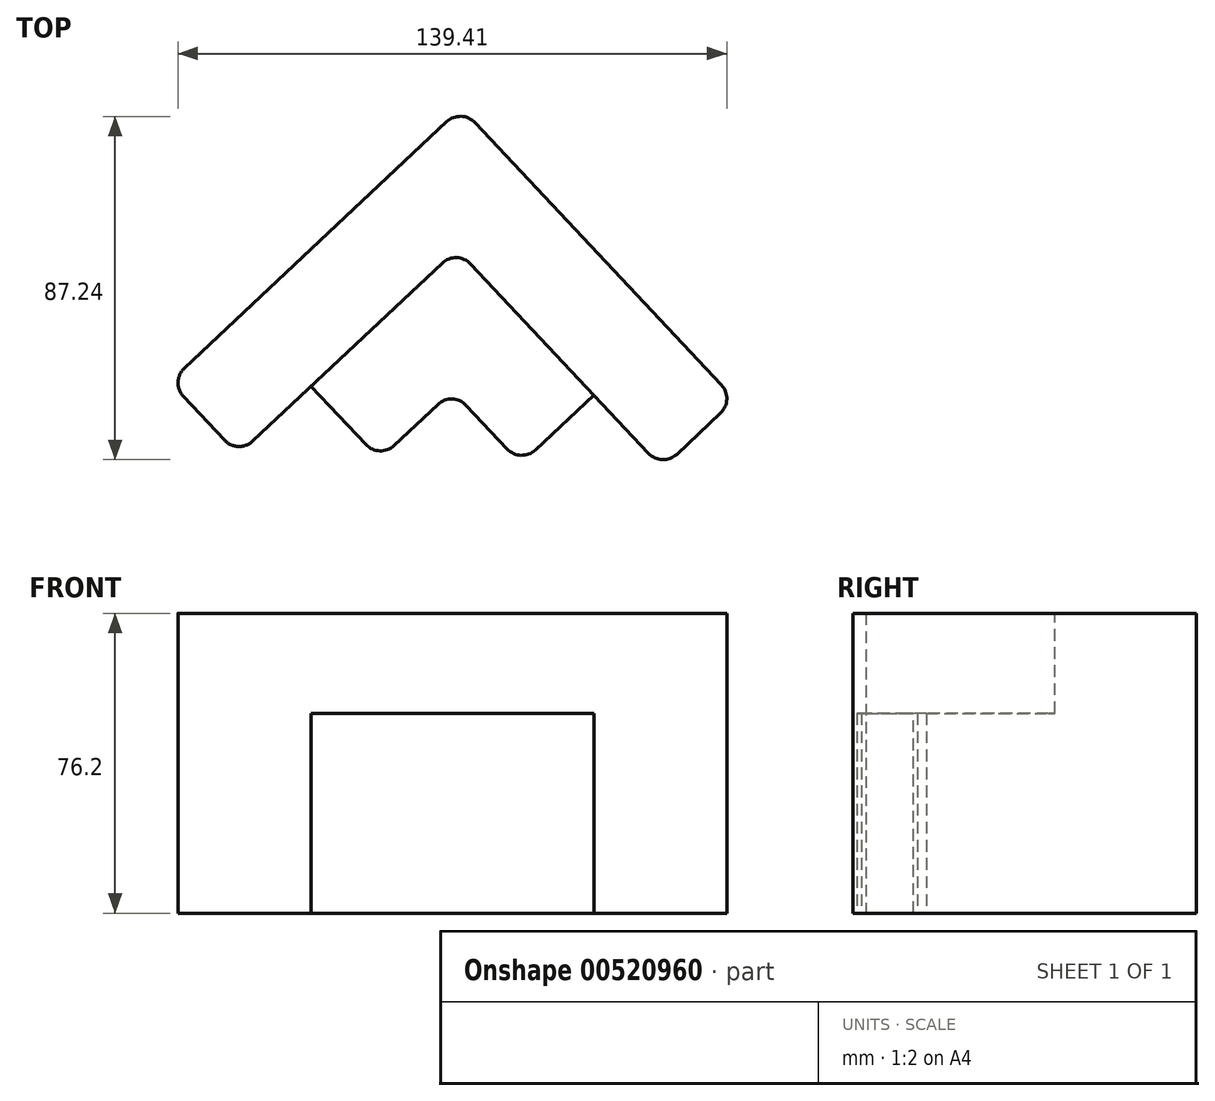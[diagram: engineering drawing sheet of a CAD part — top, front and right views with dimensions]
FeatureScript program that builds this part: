
annotation { "Feature Type Name" : "Feature", "Feature Type Description" : "" }
export const myFeature = defineFeature(function(context is Context, id is Id, definition is map)
    precondition{}
    {
        {
            var Q0;
            Q0=qCreatedBy(makeId("Top.planeOp"),FACE);
            var sketch = newSketch(context, id + "F0", { "sketchPlane" : qUnion([Q0])});
            skLineSegment(sketch, "E0", {"start": v(0, 53.43) * mm, "end": v(69.56, -20.62) * mm});
            skLineSegment(sketch, "E1", {"start": v(0, 53.43) * mm, "end": v(-74.05, -16.13) * mm});
            skLineSegment(sketch, "E2", {"start": v(169.5, -71.15) * mm, "end": v(169.5, -71.15) * mm});
            skLineSegment(sketch, "E3", {"start": v(-74.05, -16.13) * mm, "end": v(-56.66, -34.64) * mm});
            skLineSegment(sketch, "E4", {"start": v(-56.66, -34.64) * mm, "end": v(-38.15, -17.25) * mm});
            skLineSegment(sketch, "E5", {"start": v(-38.15, -17.25) * mm, "end": v(-20.76, -35.76) * mm});
            skLineSegment(sketch, "E6", {"start": v(-20.76, -35.76) * mm, "end": v(-2.24, -18.37) * mm});
            skLineSegment(sketch, "E7", {"start": v(-2.24, -18.37) * mm, "end": v(15.15, -36.89) * mm});
            skLineSegment(sketch, "E8", {"start": v(15.15, -36.89) * mm, "end": v(33.66, -19.5) * mm});
            skLineSegment(sketch, "E9", {"start": v(33.66, -19.5) * mm, "end": v(51.05, -38) * mm});
            skLineSegment(sketch, "E10", {"start": v(69.56, -20.62) * mm, "end": v(51.05, -38) * mm});
            skSolve(sketch);
        }
        {
            var Q0;
            Q0=makeQuery(id+"F0.imprint","IMPRINT",FACE,{"disambiguationData":[TD([[makeQuery(id+"F0.imprint","IMPRINT",EDGE,{"derivedFrom":sQuery(id+"F0.wireOp",EDGE,"E0")}),-1.0]])]});
            extrude(context, id + "F1", {"entities" : qUnion([Q0]), "depth" : 25.4 * mm, "offsetDistance" : 25.4 * mm});
        }
        {
            var Q0;
            Q0=makeQuery(id+"F1.opExtrude","CAP_FACE",FACE,{"disambiguationData":[OSD([sQuery(id+"F0.wireOp",EDGE,"E0"),sQuery(id+"F0.wireOp",EDGE,"E1"),sQuery(id+"F0.wireOp",EDGE,"E3"),sQuery(id+"F0.wireOp",EDGE,"E4"),sQuery(id+"F0.wireOp",EDGE,"E5"),sQuery(id+"F0.wireOp",EDGE,"E6"),sQuery(id+"F0.wireOp",EDGE,"E7"),sQuery(id+"F0.wireOp",EDGE,"E8"),sQuery(id+"F0.wireOp",EDGE,"E9"),sQuery(id+"F0.wireOp",EDGE,"E10")])],"isStart":false});
            var sketch = newSketch(context, id + "F2", { "sketchPlane" : qUnion([Q0])});
            skLineSegment(sketch, "E11", {"start": v(-38.15, -17.25) * mm, "end": v(-1.12, 17.53) * mm});
            skLineSegment(sketch, "E12", {"start": v(-1.12, 17.53) * mm, "end": v(33.66, -19.5) * mm});
            skSolve(sketch);
        }
        {
            var Q0;
            Q0=makeQuery(id+"F2.imprint","IMPRINT",FACE,{"disambiguationData":[TD([[makeQuery(id+"F2.imprint","IMPRINT",EDGE,{"derivedFrom":sQuery(id+"F2.wireOp",EDGE,"E11")}),-1.0]])]});
            extrude(context, id + "F3", {"entities" : qUnion([Q0]), "operationType" : NewBodyOperationType.ADD, "depth" : 25.4 * mm, "offsetDistance" : 25.4 * mm});
        }
        {
            var Q0;
            Q0=makeQuery(id+"F1.opExtrude","CAP_FACE",FACE,{"disambiguationData":[OSD([sQuery(id+"F0.wireOp",EDGE,"E0"),sQuery(id+"F0.wireOp",EDGE,"E1"),sQuery(id+"F0.wireOp",EDGE,"E3"),sQuery(id+"F0.wireOp",EDGE,"E4"),sQuery(id+"F0.wireOp",EDGE,"E5"),sQuery(id+"F0.wireOp",EDGE,"E6"),sQuery(id+"F0.wireOp",EDGE,"E7"),sQuery(id+"F0.wireOp",EDGE,"E8"),sQuery(id+"F0.wireOp",EDGE,"E9"),sQuery(id+"F0.wireOp",EDGE,"E10")])],"isStart":false});
            var sketch = newSketch(context, id + "F4", { "sketchPlane" : qUnion([Q0])});
            skSolve(sketch);
        }
        {
            var Q0;
            Q0=makeQuery(id+"F4.imprint","IMPRINT",FACE,{"disambiguationData":[TD([[makeQuery(id+"F4.imprint","IMPRINT",EDGE,{"derivedFrom":makeQuery(id+"F1.opExtrude","CAP_EDGE",EDGE,{"disambiguationData":[OSD([sQuery(id+"F0.wireOp",EDGE,"E0")])],"isStart":false})}),-1.0]])]});
            extrude(context, id + "F5", {"entities" : qUnion([Q0]), "operationType" : NewBodyOperationType.ADD, "depth" : 50.8 * mm, "offsetDistance" : 25.4 * mm});
        }
        {
            var Q0;
            Q0=makeQuery(id+"F5.opExtrude","SWEPT_EDGE",EDGE,{"disambiguationData":[OSD([sQuery(id+"F2.wireOp",EDGE,"E11"),sQuery(id+"F2.wireOp",EDGE,"E12")])]});
            fillet(context, id + "F6", {"entities" : qUnion([Q0]), "radius" : 5.08 * mm, "tangentPropagation" : true, "allowEdgeOverflow" : false});
        }
        {
            var Q0;
            {var subQ0=sQuery(id+"F0.wireOp",EDGE,"E7");var subQ1=sQuery(id+"F0.wireOp",EDGE,"E6");Q0=makeQuery(id+"F3.boolean.opBoolean","MERGE",EDGE,{"derivedFrom":[makeQuery(id+"F1.opExtrude","SWEPT_EDGE",EDGE,{"disambiguationData":[OSD([subQ1,subQ0])]}),makeQuery(id+"F3.opExtrude","SWEPT_EDGE",EDGE,{"disambiguationData":[OSD([subQ1,subQ0])]})]});}
            fillet(context, id + "F7", {"entities" : qUnion([Q0]), "radius" : 5.08 * mm, "tangentPropagation" : true, "allowEdgeOverflow" : false});
        }
        {
            var Q0;
            {var subQ0=sQuery(id+"F0.wireOp",EDGE,"E8");var subQ1=sQuery(id+"F0.wireOp",EDGE,"E7");Q0=makeQuery(id+"F3.boolean.opBoolean","MERGE",EDGE,{"derivedFrom":[makeQuery(id+"F1.opExtrude","SWEPT_EDGE",EDGE,{"disambiguationData":[OSD([subQ1,subQ0])]}),makeQuery(id+"F3.opExtrude","SWEPT_EDGE",EDGE,{"disambiguationData":[OSD([subQ1,subQ0])]})]});}
            fillet(context, id + "F8", {"entities" : qUnion([Q0]), "radius" : 5.08 * mm, "tangentPropagation" : true, "allowEdgeOverflow" : false});
        }
        {
            var Q0;
            {var subQ0=sQuery(id+"F0.wireOp",EDGE,"E6");var subQ1=sQuery(id+"F0.wireOp",EDGE,"E5");Q0=makeQuery(id+"F3.boolean.opBoolean","MERGE",EDGE,{"derivedFrom":[makeQuery(id+"F1.opExtrude","SWEPT_EDGE",EDGE,{"disambiguationData":[OSD([subQ1,subQ0])]}),makeQuery(id+"F3.opExtrude","SWEPT_EDGE",EDGE,{"disambiguationData":[OSD([subQ1,subQ0])]})]});}
            fillet(context, id + "F9", {"entities" : qUnion([Q0]), "radius" : 5.08 * mm, "tangentPropagation" : true, "allowEdgeOverflow" : false});
        }
        {
            var Q0;
            {var subQ0=sQuery(id+"F0.wireOp",EDGE,"E1");var subQ1=sQuery(id+"F0.wireOp",EDGE,"E0");Q0=makeQuery(id+"F5.boolean.opBoolean","MERGE",EDGE,{"derivedFrom":[makeQuery(id+"F1.opExtrude","SWEPT_EDGE",EDGE,{"disambiguationData":[OSD([subQ1,subQ0])]}),makeQuery(id+"F5.opExtrude","SWEPT_EDGE",EDGE,{"disambiguationData":[OSD([subQ1,subQ0])]})]});}
            fillet(context, id + "F10", {"entities" : qUnion([Q0]), "radius" : 5.08 * mm, "tangentPropagation" : true, "allowEdgeOverflow" : false});
        }
        {
            var Q0;
            {var subQ0=sQuery(id+"F0.wireOp",EDGE,"E3");var subQ1=sQuery(id+"F0.wireOp",EDGE,"E1");Q0=makeQuery(id+"F5.boolean.opBoolean","MERGE",EDGE,{"derivedFrom":[makeQuery(id+"F1.opExtrude","SWEPT_EDGE",EDGE,{"disambiguationData":[OSD([subQ1,subQ0])]}),makeQuery(id+"F5.opExtrude","SWEPT_EDGE",EDGE,{"disambiguationData":[OSD([subQ1,subQ0])]})]});}
            fillet(context, id + "F11", {"entities" : qUnion([Q0]), "radius" : 5.08 * mm, "tangentPropagation" : true, "allowEdgeOverflow" : false});
        }
        {
            var Q0;
            {var subQ0=sQuery(id+"F0.wireOp",EDGE,"E10");var subQ1=sQuery(id+"F0.wireOp",EDGE,"E0");Q0=makeQuery(id+"F5.boolean.opBoolean","MERGE",EDGE,{"derivedFrom":[makeQuery(id+"F1.opExtrude","SWEPT_EDGE",EDGE,{"disambiguationData":[OSD([subQ1,subQ0])]}),makeQuery(id+"F5.opExtrude","SWEPT_EDGE",EDGE,{"disambiguationData":[OSD([subQ1,subQ0])]})]});}
            fillet(context, id + "F12", {"entities" : qUnion([Q0]), "radius" : 5.08 * mm, "tangentPropagation" : true, "allowEdgeOverflow" : false});
        }
        {
            var Q0;
            {var subQ0=sQuery(id+"F0.wireOp",EDGE,"E4");var subQ1=sQuery(id+"F0.wireOp",EDGE,"E3");Q0=makeQuery(id+"F5.boolean.opBoolean","MERGE",EDGE,{"derivedFrom":[makeQuery(id+"F1.opExtrude","SWEPT_EDGE",EDGE,{"disambiguationData":[OSD([subQ1,subQ0])]}),makeQuery(id+"F5.opExtrude","SWEPT_EDGE",EDGE,{"disambiguationData":[OSD([subQ1,subQ0])]})]});}
            fillet(context, id + "F13", {"entities" : qUnion([Q0]), "radius" : 5.08 * mm, "tangentPropagation" : true, "allowEdgeOverflow" : false});
        }
        {
            var Q0;
            {var subQ0=sQuery(id+"F0.wireOp",EDGE,"E10");var subQ1=sQuery(id+"F0.wireOp",EDGE,"E9");Q0=makeQuery(id+"F5.boolean.opBoolean","MERGE",EDGE,{"derivedFrom":[makeQuery(id+"F1.opExtrude","SWEPT_EDGE",EDGE,{"disambiguationData":[OSD([subQ1,subQ0])]}),makeQuery(id+"F5.opExtrude","SWEPT_EDGE",EDGE,{"disambiguationData":[OSD([subQ1,subQ0])]})]});}
            fillet(context, id + "F14", {"entities" : qUnion([Q0]), "radius" : 5.08 * mm, "tangentPropagation" : true, "allowEdgeOverflow" : false});
        }
    });
